# Revit family: Pro_Stool_Sandler_KERN 0320
name_source: partatom
category: Furniture
units: mm (PartAtom-declared; Revit-internal decimal feet)

## family parameters
Always vertical = Yes
Cut with Voids When Loaded = No
OmniClass Number = 23.40.20.00
OmniClass Title = General Furniture and Specialties
Render Appearance Source = Family Geometry
Room Calculation Point = No
Shared = No
Work Plane-Based = No

## types (1)
- Kern 0320
    Default Elevation = 0 mm  [stored 0 ft]
    Depth = 1000 mm  [stored 3.28084 ft]
    Description = Medium round ottoman measuring 39.4"/100cm in diameter, with epoxy-painted legs. 99% recyclable.
    Height = 430 mm  [stored 1.41076 ft]
    Manufacturer = Sandler
    Model = Kern 0320
    URL = https://www.sandlerseating.com
    Width = 1000 mm  [stored 3.28084 ft]

note: [stored X ft] marks values corroborated as IEEE doubles in the binary element streams (Revit-internal decimal feet)

## geometry (parser evidence)
native form markers: Sweep x7
no freeform markers — native parametric forms only
